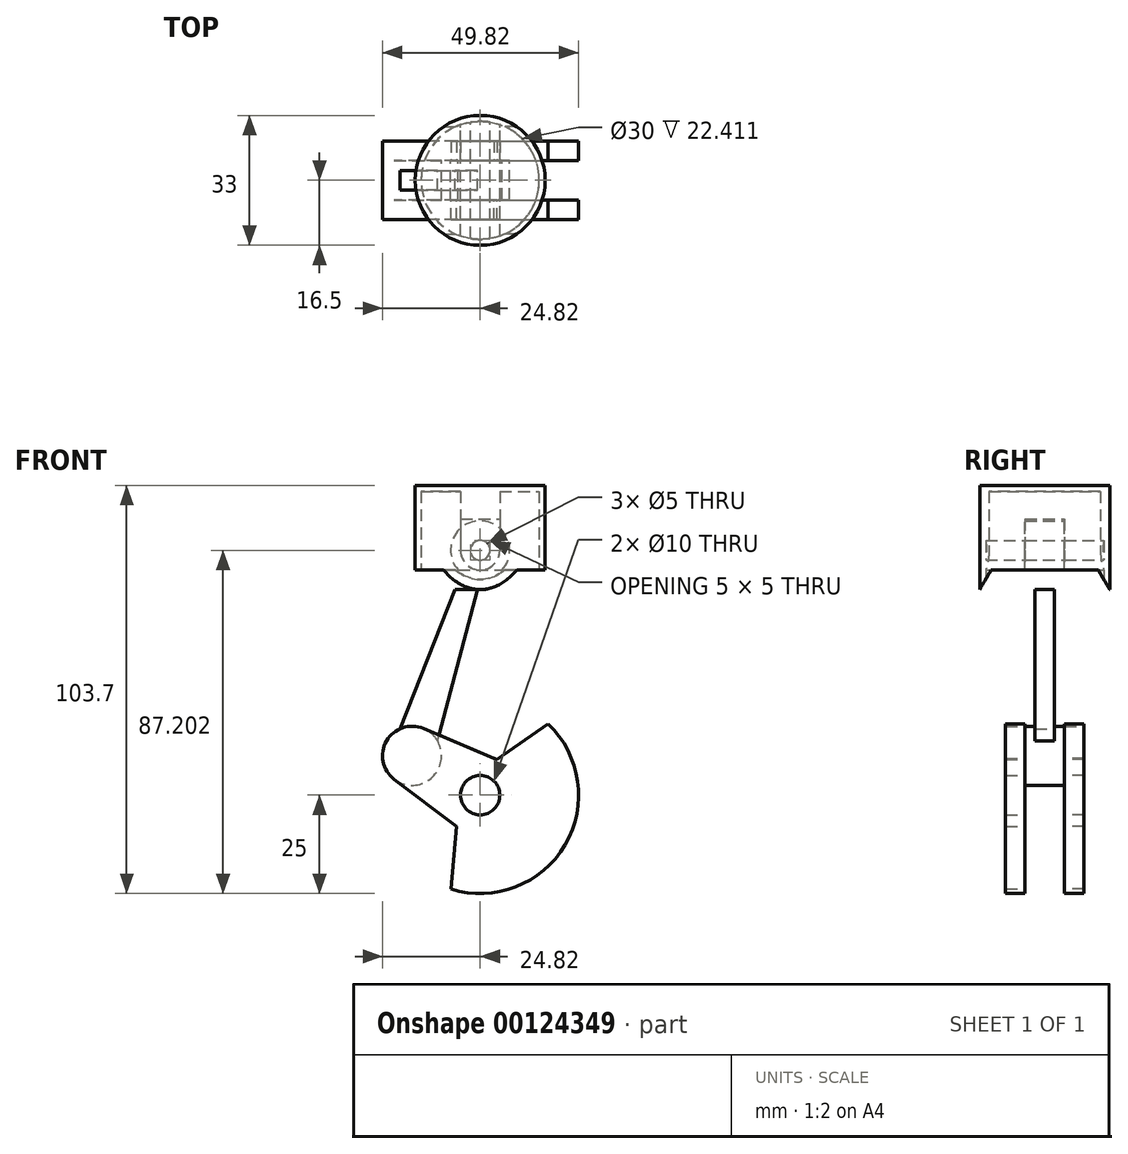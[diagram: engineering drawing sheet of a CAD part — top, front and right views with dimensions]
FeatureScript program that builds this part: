
annotation { "Feature Type Name" : "Feature", "Feature Type Description" : "" }
export const myFeature = defineFeature(function(context is Context, id is Id, definition is map)
    precondition{}
    {
        {
            var Q0;
            Q0=qCreatedBy(makeId("Front.planeOp"),FACE);
            var sketch = newSketch(context, id + "F0", { "sketchPlane" : qUnion([Q0])});
            skLineSegment(sketch, "E0", {"start": v(0, 0) * mm, "end": v(0, 94.92) * mm, "construction": true});
            skLineSegment(sketch, "E1", {"start": v(-54.43, 0) * mm, "end": v(54.43, 0) * mm, "construction": true});
            skLineSegment(sketch, "E2", {"start": v(-54.43, 50) * mm, "end": v(54.43, 50) * mm, "construction": true});
            skLineSegment(sketch, "E3", {"start": v(-54.43, 90) * mm, "end": v(54.43, 90) * mm, "construction": true});
            skLineSegment(sketch, "E4.bottom", {"start": v(15, 52.2) * mm, "end": v(-15, 52.2) * mm});
            skLineSegment(sketch, "E4.top", {"start": v(15, 77.2) * mm, "end": v(-15, 77.2) * mm});
            skLineSegment(sketch, "E4.left", {"start": v(15, 52.2) * mm, "end": v(15, 77.2) * mm});
            skLineSegment(sketch, "E4.right", {"start": v(-15, 52.2) * mm, "end": v(-15, 77.2) * mm});
            skPoint(sketch, "E4.middle", {"position": v(0, 64.7) * mm});
            skLineSegment(sketch, "E5", {"start": v(-5, 77.2) * mm, "end": v(-5, 70.2) * mm});
            skLineSegment(sketch, "E6", {"start": v(-5, 70.2) * mm, "end": v(5, 70.2) * mm});
            skLineSegment(sketch, "E7", {"start": v(5, 70.2) * mm, "end": v(5, 77.2) * mm});
            skLineSegment(sketch, "E8", {"start": v(-5, 70.2) * mm, "end": v(-5, 62.2) * mm});
            skLineSegment(sketch, "E9", {"start": v(5, 70.2) * mm, "end": v(5, 62.2) * mm});
            skArc(sketch, "E10", {"start": v(-5, 62.2) * mm, "mid": v(0, 57.2) * mm, "end": v(5, 62.2) * mm});
            skCircle(sketch, "E11", {"center": v(0, 62.2) * mm, "radius": 2.5 * mm});
            skLineSegment(sketch, "E12", {"start": v(0, 62.2) * mm, "end": v(-17.32, 10) * mm});
            skLineSegment(sketch, "E13", {"start": v(0, 0) * mm, "end": v(-17.32, 10) * mm});
            skSolve(sketch);
        }
        {
            var Q0;
            Q0=qCreatedBy(makeId("Front.planeOp"),FACE);
            var sketch = newSketch(context, id + "F1", { "sketchPlane" : qUnion([Q0])});
            skLineSegment(sketch, "E14", {"start": v(0, 77.2) * mm, "end": v(15, 77.2) * mm});
            skLineSegment(sketch, "E15", {"start": v(15, 77.2) * mm, "end": v(15, 52.2) * mm});
            skLineSegment(sketch, "E16", {"start": v(15, 52.2) * mm, "end": v(0, 52.2) * mm});
            skLineSegment(sketch, "E17", {"start": v(0, 77.2) * mm, "end": v(0, 52.2) * mm});
            skPoint(sketch, "E18.orphan", {"position": v(-15, 77.2) * mm});
            skSolve(sketch);
        }
        {
            var Q0;
            Q0 = qSketchRegion(id + "F1", true);
            var Q1;
            Q1=sQuery(id+"F0.wireOp",EDGE,"E0");
            revolve(context, id + "F2", {"entities" : qUnion([Q0]), "axis" : qUnion([Q1]), "revolveType" : RevolveType.FULL});
        }
        {
            var Q0;
            Q0=makeQuery(id+"F2.opRevolve","SWEPT_FACE",FACE,{"disambiguationData":[OSD([sQuery(id+"F1.wireOp",EDGE,"E16")])]});
            shell(context, id + "F3", {"entities" : qUnion([Q0]), "thickness" : 1.5 * mm, "oppositeDirection" : true});
        }
        {
            var Q0;
            {var subQ0=sQuery(id+"F0.wireOp",EDGE,"E5");Q0=makeQuery(id+"F0.imprint","IMPRINT",FACE,{"disambiguationData":[TD([[makeQuery(id+"F0.imprint","IMPRINT",EDGE,{"derivedFrom":subQ0}),1.0]])]});}
            var Q1;
            Q1=makeQuery(id+"F0.imprint","IMPRINT",FACE,{"disambiguationData":[TD([[makeQuery(id+"F0.imprint","IMPRINT",EDGE,{"derivedFrom":sQuery(id+"F0.wireOp",EDGE,"E6")}),-1.0]])]});
            var Q2;
            Q2=makeQuery(id+"F3.opShell","OFFSET_FACE",FACE,{"disambiguationData":[OSD([sQuery(id+"F1.wireOp",EDGE,"E15")])]});
            var Q3;
            Q3=makeQuery(id+"F3.opShell","OFFSET_FACE",FACE,{"disambiguationData":[OSD([sQuery(id+"F1.wireOp",EDGE,"E15")])]});
            extrude(context, id + "F4", {"entities" : qUnion([Q0, Q1]), "operationType" : NewBodyOperationType.ADD, "endBound" : BoundingType.UP_TO_SURFACE, "endBoundEntityFace" : qUnion([Q2]), "depth" : 25 * mm, "hasSecondDirection" : true, "secondDirectionBound" : SecondDirectionBoundingType.UP_TO_SURFACE, "secondDirectionOppositeDirection" : true, "secondDirectionBoundEntityFace" : qUnion([Q3]), "secondDirectionDepth" : 25 * mm});
        }
        {
            var Q0;
            Q0=qCreatedBy(makeId("Front.planeOp"),FACE);
            var sketch = newSketch(context, id + "F5", { "sketchPlane" : qUnion([Q0])});
            skCircle(sketch, "E19", {"center": v(-17.32, 10) * mm, "radius": 4 * mm});
            skCircle(sketch, "E20", {"center": v(-17.32, 10) * mm, "radius": 7.5 * mm});
            skCircle(sketch, "E21", {"center": v(0, 62.2) * mm, "radius": 7.5 * mm});
            skCircle(sketch, "E22", {"center": v(0, 62.2) * mm, "radius": 2.5 * mm});
            skLineSegment(sketch, "E23", {"start": v(15, 52.2) * mm, "end": v(-15, 52.2) * mm});
            skLineSegment(sketch, "E24", {"start": v(-20.3, 16.88) * mm, "end": v(-4.71, 56.37) * mm});
            skLineSegment(sketch, "E25", {"start": v(-10.81, 13.73) * mm, "end": v(0, 54.7) * mm});
            skSolve(sketch);
        }
        {
            var Q0;
            Q0=makeQuery(id+"F0.imprint","IMPRINT",FACE,{"disambiguationData":[TD([[makeQuery(id+"F0.imprint","IMPRINT",EDGE,{"derivedFrom":sQuery(id+"F0.wireOp",EDGE,"E6")}),-1.0]])]});
            extrude(context, id + "F6", {"entities" : qUnion([Q0]), "operationType" : NewBodyOperationType.REMOVE, "endBound" : BoundingType.SYMMETRIC, "depth" : 10 * mm});
        }
        {
            var Q0;
            Q0=qCreatedBy(makeId("Front.planeOp"),FACE);
            var sketch = newSketch(context, id + "F7", { "sketchPlane" : qUnion([Q0])});
            skCircle(sketch, "E26", {"center": v(0, 0) * mm, "radius": 5 * mm});
            skCircle(sketch, "E27", {"center": v(0, 0) * mm, "radius": 10 * mm});
            skCircle(sketch, "E28", {"center": v(-17.32, 10) * mm, "radius": 4 * mm});
            skCircle(sketch, "E29", {"center": v(-17.32, 10) * mm, "radius": 7.5 * mm});
            skLineSegment(sketch, "E30", {"start": v(0, 0) * mm, "end": v(19.13, -11.04) * mm, "construction": true});
            skLineSegment(sketch, "E31", {"start": v(4.23, 9.06) * mm, "end": v(17.2, 18.15) * mm});
            skLineSegment(sketch, "E32", {"start": v(-6.04, -7.97) * mm, "end": v(-7.43, -23.87) * mm});
            skLineSegment(sketch, "E33", {"start": v(-6.04, -7.97) * mm, "end": v(-21.85, 4.02) * mm});
            skLineSegment(sketch, "E34", {"start": v(4.23, 9.06) * mm, "end": v(-14.4, 16.91) * mm});
            skArc(sketch, "E35", {"start": v(-7.43, -23.87) * mm, "mid": v(21.57, -12.64) * mm, "end": v(17.2, 18.15) * mm});
            skSolve(sketch);
        }
        {
            var Q0;
            Q0=makeQuery(id+"F5.imprint","IMPRINT",FACE,{"disambiguationData":[TD([[makeQuery(id+"F5.imprint","IMPRINT",EDGE,{"derivedFrom":sQuery(id+"F5.wireOp",EDGE,"E22")}),-1.0]])]});
            var Q1;
            Q1=makeQuery(id+"F7.imprint","IMPRINT",FACE,{"disambiguationData":[TD([[makeQuery(id+"F7.imprint","IMPRINT",EDGE,{"derivedFrom":sQuery(id+"F7.wireOp",EDGE,"E28")}),-1.0]])]});
            var Q2;
            Q2=sQuery(id+"F5.wireOp",EDGE,"E21");
            var Q3;
            Q3=makeQuery(id+"F6.boolean.opBoolean","COPY",FACE,{"derivedFrom":makeQuery(id+"F6.opExtrude","CAP_FACE",FACE,{"disambiguationData":[OSD([sQuery(id+"F0.wireOp",EDGE,"E6"),sQuery(id+"F0.wireOp",EDGE,"E8"),sQuery(id+"F0.wireOp",EDGE,"E9"),sQuery(id+"F0.wireOp",EDGE,"E10"),sQuery(id+"F0.wireOp",EDGE,"E11")])],"isStart":false})});
            var Q4;
            Q4=makeQuery(id+"F6.boolean.opBoolean","COPY",FACE,{"derivedFrom":makeQuery(id+"F6.opExtrude","CAP_FACE",FACE,{"disambiguationData":[OSD([sQuery(id+"F0.wireOp",EDGE,"E6"),sQuery(id+"F0.wireOp",EDGE,"E8"),sQuery(id+"F0.wireOp",EDGE,"E9"),sQuery(id+"F0.wireOp",EDGE,"E10"),sQuery(id+"F0.wireOp",EDGE,"E11")])],"isStart":true})});
            extrude(context, id + "F8", {"entities" : qUnion([Q0, Q1]), "surfaceEntities" : qUnion([Q2]), "endBound" : BoundingType.UP_TO_SURFACE, "endBoundEntityFace" : qUnion([Q3]), "depth" : 25 * mm, "hasSecondDirection" : true, "secondDirectionBound" : SecondDirectionBoundingType.UP_TO_SURFACE, "secondDirectionOppositeDirection" : true, "secondDirectionBoundEntityFace" : qUnion([Q4]), "secondDirectionDepth" : 25 * mm});
        }
        {
            var Q0;
            {var subQ0=sQuery(id+"F5.wireOp",EDGE,"E24");var subQ1=sQuery(id+"F5.wireOp",EDGE,"E20");var subQ2=makeQuery(id+"F5.imprint","INTERSECT",VERTEX,{"derivedFrom":[subQ1,subQ0]});Q0=makeQuery(id+"F5.imprint","IMPRINT",FACE,{"disambiguationData":[TD([[makeQuery(id+"F5.imprint","IMPRINT",EDGE,{"disambiguationData":[TD([[subQ2,1.0]])],"derivedFrom":subQ1}),-1.0]])]});}
            var Q1;
            {var subQ0=sQuery(id+"F5.wireOp",EDGE,"E24");var subQ1=sQuery(id+"F5.wireOp",EDGE,"E21");var subQ2=makeQuery(id+"F5.imprint","INTERSECT",VERTEX,{"derivedFrom":[subQ1,subQ0]});Q1=makeQuery(id+"F5.imprint","IMPRINT",FACE,{"disambiguationData":[TD([[makeQuery(id+"F5.imprint","IMPRINT",EDGE,{"disambiguationData":[TD([[subQ2,-1.0]])],"derivedFrom":subQ1}),-1.0]])]});}
            extrude(context, id + "F9", {"entities" : qUnion([Q0, Q1]), "operationType" : NewBodyOperationType.ADD, "endBound" : BoundingType.SYMMETRIC, "depth" : 5 * mm});
        }
        {
            var Q0;
            Q0 = qSketchRegion(id + "F7", true);
            extrude(context, id + "F10", {"entities" : qUnion([Q0]), "oppositeDirection" : true, "depth" : 10 * mm, "hasSecondDirection" : true, "secondDirectionOppositeDirection" : true, "secondDirectionDepth" : 5 * mm});
        }
        {
            var Q0;
            Q0=makeQuery(id+"F10.opExtrude","SWEPT_BODY",BODY,{"disambiguationData":[OSD([sQuery(id+"F7.wireOp",EDGE,"E26"),sQuery(id+"F7.wireOp",EDGE,"E27"),sQuery(id+"F7.wireOp",EDGE,"E28"),sQuery(id+"F7.wireOp",EDGE,"E29"),sQuery(id+"F7.wireOp",EDGE,"E31"),sQuery(id+"F7.wireOp",EDGE,"E32"),sQuery(id+"F7.wireOp",EDGE,"E33"),sQuery(id+"F7.wireOp",EDGE,"E34"),sQuery(id+"F7.wireOp",EDGE,"E35")])]});
            var Q1;
            Q1=qCreatedBy(makeId("Front.planeOp"),FACE);
            mirror(context, id + "F11", {"entities" : qUnion([Q0]), "mirrorPlane" : qUnion([Q1])});
        }
        {
            var Q0;
            Q0=makeQuery(id+"F7.imprint","IMPRINT",FACE,{"disambiguationData":[TD([[makeQuery(id+"F7.imprint","IMPRINT",EDGE,{"derivedFrom":sQuery(id+"F7.wireOp",EDGE,"E28")}),1.0]])]});
            extrude(context, id + "F12", {"entities" : qUnion([Q0]), "operationType" : NewBodyOperationType.ADD, "endBound" : BoundingType.SYMMETRIC, "depth" : 20 * mm});
        }
        {
            var Q0;
            Q0=qCreatedBy(makeId("Right.planeOp"),FACE);
            var sketch = newSketch(context, id + "F13", { "sketchPlane" : qUnion([Q0])});
            skLineSegment(sketch, "E36", {"start": v(16.5, 52.2) * mm, "end": v(-16.5, 52.2) * mm});
            skLineSegment(sketch, "E37", {"start": v(-16.5, 52.2) * mm, "end": v(-13.61, 57.2) * mm});
            skLineSegment(sketch, "E38", {"start": v(-13.61, 57.2) * mm, "end": v(13.61, 57.2) * mm});
            skLineSegment(sketch, "E39", {"start": v(13.61, 57.2) * mm, "end": v(16.5, 52.2) * mm});
            skSolve(sketch);
        }
        {
            var Q0;
            Q0=makeQuery(id+"F13.imprint","IMPRINT",FACE,{"disambiguationData":[TD([[makeQuery(id+"F13.imprint","IMPRINT",EDGE,{"derivedFrom":sQuery(id+"F13.wireOp",EDGE,"E36")}),-1.0]])]});
            var Q1;
            Q1=makeQuery(id+"F2.opRevolve","SWEPT_FACE",FACE,{"disambiguationData":[OSD([sQuery(id+"F1.wireOp",EDGE,"E15")])]});
            var Q2;
            Q2=makeQuery(id+"F4.boolean.opBoolean","SPLIT",FACE,{"disambiguationData":[TD([makeQuery(id+"F2.opRevolve","SWEPT_FACE",FACE,{"disambiguationData":[OSD([sQuery(id+"F1.wireOp",EDGE,"E16")])]}),makeQuery(id+"F3.opShell","OFFSET_FACE",FACE,{"disambiguationData":[OSD([sQuery(id+"F1.wireOp",EDGE,"E14")])]}),makeQuery(id+"F4.opExtrude","SWEPT_FACE",FACE,{"disambiguationData":[OSD([sQuery(id+"F0.wireOp",EDGE,"E5"),sQuery(id+"F0.wireOp",EDGE,"E8")])]}),makeQuery(id+"F4.opExtrude","SWEPT_FACE",FACE,{"disambiguationData":[OSD([sQuery(id+"F0.wireOp",EDGE,"E7"),sQuery(id+"F0.wireOp",EDGE,"E9")])]}),makeQuery(id+"F4.opExtrude","SWEPT_FACE",FACE,{"disambiguationData":[OSD([sQuery(id+"F0.wireOp",EDGE,"E10")])]})])],"derivedFrom":makeQuery(id+"F3.opShell","OFFSET_FACE",FACE,{"disambiguationData":[OSD([sQuery(id+"F1.wireOp",EDGE,"E15")])]})});
            extrude(context, id + "F14", {"entities" : qUnion([Q0]), "operationType" : NewBodyOperationType.REMOVE, "endBound" : BoundingType.UP_TO_SURFACE, "oppositeDirection" : true, "endBoundEntityFace" : qUnion([Q1]), "depth" : 25 * mm, "hasSecondDirection" : true, "secondDirectionOppositeDirection" : false, "secondDirectionBoundEntityFace" : qUnion([Q2]), "secondDirectionDepth" : .5 * mm});
        }
        {
            var Q0;
            Q0=makeQuery(id+"F13.imprint","IMPRINT",FACE,{"disambiguationData":[TD([[makeQuery(id+"F13.imprint","IMPRINT",EDGE,{"derivedFrom":sQuery(id+"F13.wireOp",EDGE,"E36")}),-1.0]])]});
            var Q1;
            Q1=makeQuery(id+"F2.opRevolve","SWEPT_FACE",FACE,{"disambiguationData":[OSD([sQuery(id+"F1.wireOp",EDGE,"E15")])]});
            extrude(context, id + "F15", {"entities" : qUnion([Q0]), "operationType" : NewBodyOperationType.REMOVE, "endBound" : BoundingType.UP_TO_SURFACE, "endBoundEntityFace" : qUnion([Q1]), "depth" : 25 * mm, "hasSecondDirection" : true, "secondDirectionOppositeDirection" : true, "secondDirectionDepth" : .5 * mm});
        }
    });
